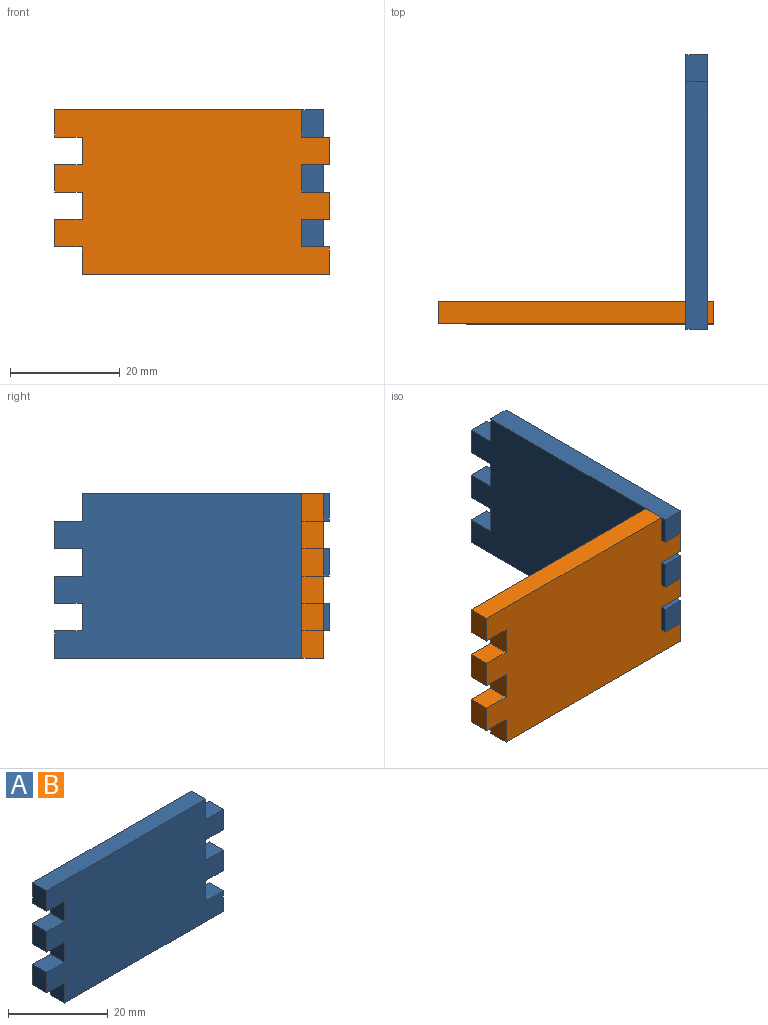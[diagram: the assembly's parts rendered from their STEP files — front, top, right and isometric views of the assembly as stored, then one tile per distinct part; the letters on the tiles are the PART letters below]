
ASSEMBLY  parts=2 mates=1
PART A: 26 faces, bbox 50x4x30 mm
  f0: plane 45x4mm, normal (0,0,1), area 180mm2, adj f1,f23,f24,f25
  f1: plane 5x4mm, normal (-1,0,0), area 20mm2, adj f0,f2,f24,f25
  f2: plane 5x4mm, normal (0,0,-1), area 20mm2, adj f1,f3,f24,f25
  f3: plane 5x4mm, normal (-1,0,0), area 20mm2, adj f2,f4,f24,f25
  f4: plane 5x4mm, normal (0,0,1), area 20mm2, adj f3,f5,f24,f25
  f5: plane 5x4mm, normal (-1,0,0), area 20mm2, adj f4,f6,f24,f25
  f6: plane 5x4mm, normal (0,0,-1), area 20mm2, adj f5,f7,f24,f25
  f7: plane 5x4mm, normal (-1,0,0), area 20mm2, adj f6,f8,f24,f25
  f8: plane 5x4mm, normal (0,0,1), area 20mm2, adj f7,f9,f24,f25
  f9: plane 5x4mm, normal (-1,0,0), area 20mm2, adj f8,f10,f24,f25
  f10: plane 5x4mm, normal (0,0,-1), area 20mm2, adj f9,f11,f24,f25
  f11: plane 5x4mm, normal (-1,0,0), area 20mm2, adj f10,f12,f24,f25
  f12: plane 45x4mm, normal (0,0,-1), area 180mm2, adj f11,f13,f24,f25
  f13: plane 5x4mm, normal (1,0,0), area 20mm2, adj f12,f14,f24,f25
  f14: plane 5x4mm, normal (0,0,1), area 20mm2, adj f13,f15,f24,f25
  f15: plane 5x4mm, normal (1,0,0), area 20mm2, adj f14,f16,f24,f25
  f16: plane 5x4mm, normal (0,0,-1), area 20mm2, adj f15,f17,f24,f25
  f17: plane 5x4mm, normal (1,0,0), area 20mm2, adj f16,f18,f24,f25
  f18: plane 5x4mm, normal (0,0,1), area 20mm2, adj f17,f19,f24,f25
  f19: plane 5x4mm, normal (1,0,0), area 20mm2, adj f18,f20,f24,f25
  f20: plane 5x4mm, normal (0,0,-1), area 20mm2, adj f19,f21,f24,f25
  f21: plane 5x4mm, normal (1,0,0), area 20mm2, adj f20,f22,f24,f25
  f22: plane 5x4mm, normal (0,0,1), area 20mm2, adj f21,f23,f24,f25
  f23: plane 5x4mm, normal (1,0,0), area 20mm2, adj f0,f22,f24,f25
  f24: plane 50x30mm, normal (0,-1,0), area 1350mm2, adj f0,f1,f2,f3,f4,f5,f6,f7
  f25: plane 50x30mm, normal (0,1,0), area 1350mm2, adj f0,f1,f2,f3,f4,f5,f6,f7
PART B: same geometry as A
PLACE A rot(axis=(0,0,1),90deg) t=(16.48,15.69,-3.13)mm
PLACE B t=(-9.04,1.22,-3.13)mm
MATE planar A.f25 <-> B.f23  axis (-1,0,0) through (16.48,1.22,11.87)mm
